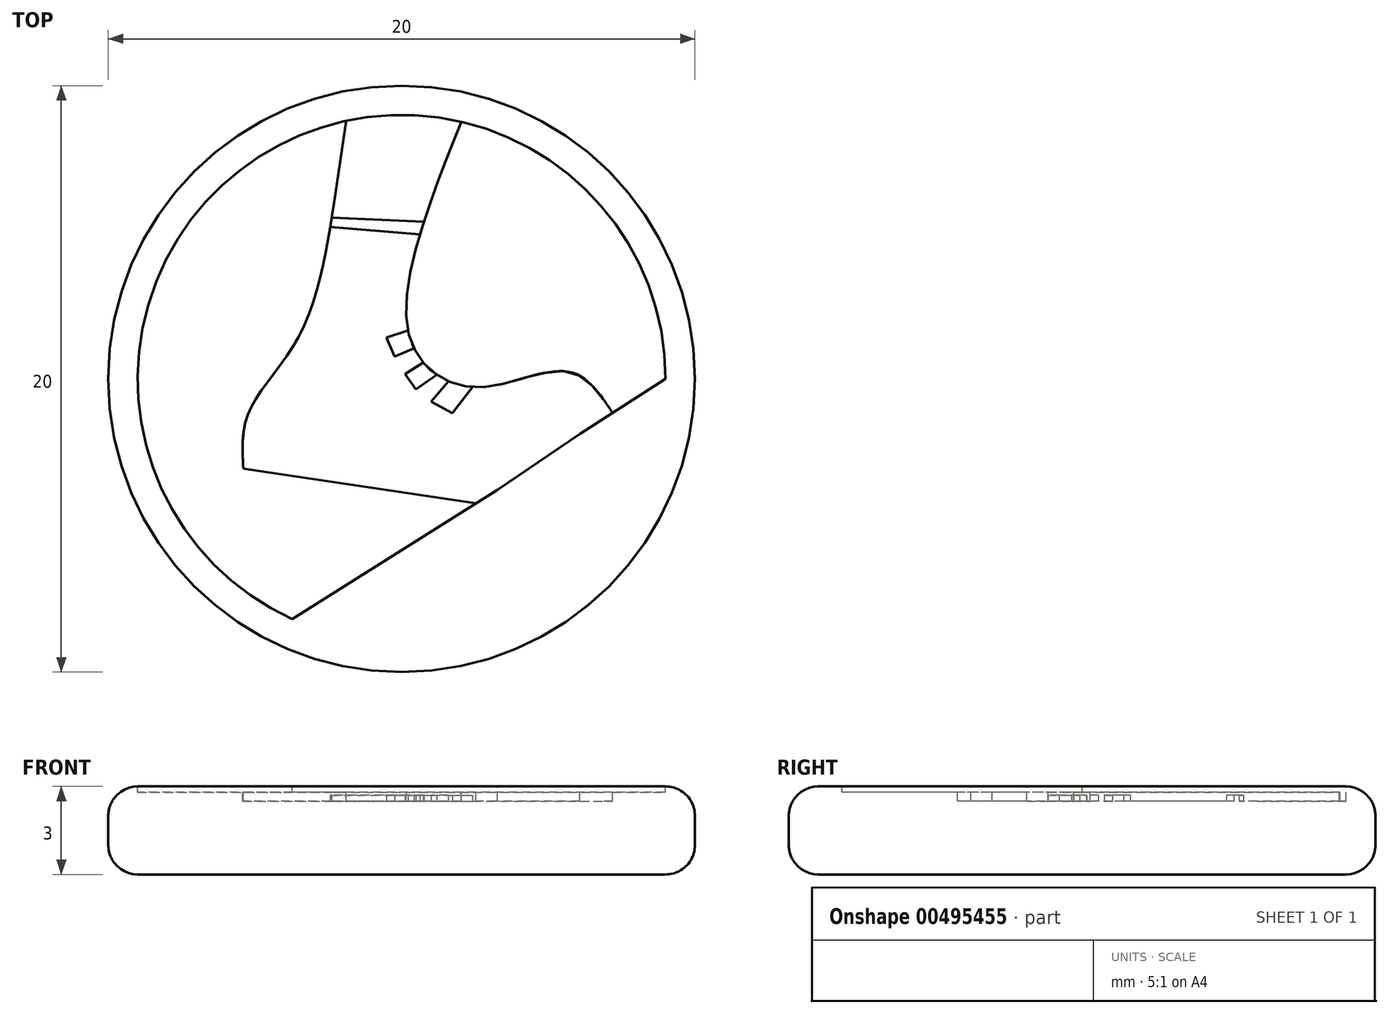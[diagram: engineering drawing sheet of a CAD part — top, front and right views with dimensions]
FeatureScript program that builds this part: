
annotation { "Feature Type Name" : "Feature", "Feature Type Description" : "" }
export const myFeature = defineFeature(function(context is Context, id is Id, definition is map)
    precondition{}
    {
        {
            var Q0;
            Q0=qCreatedBy(makeId("Top.planeOp"),FACE);
            var sketch = newSketch(context, id + "F0", { "sketchPlane" : qUnion([Q0])});
            skCircle(sketch, "E0", {"center": v(0, 0) * mm, "radius": 10 * mm});
            skSolve(sketch);
        }
        {
            var Q0;
            Q0=makeQuery(id+"F0.imprint","IMPRINT",FACE,{"disambiguationData":[TD([[makeQuery(id+"F0.imprint","IMPRINT",EDGE,{"derivedFrom":sQuery(id+"F0.wireOp",EDGE,"E0")}),1.0]])]});
            extrude(context, id + "F1", {"entities" : qUnion([Q0]), "depth" : 3 * mm});
        }
        {
            var Q0;
            Q0=makeQuery(id+"F1.opExtrude","CAP_EDGE",EDGE,{"disambiguationData":[OSD([sQuery(id+"F0.wireOp",EDGE,"E0")])],"isStart":false});
            var Q1;
            Q1=makeQuery(id+"F1.opExtrude","CAP_EDGE",EDGE,{"disambiguationData":[OSD([sQuery(id+"F0.wireOp",EDGE,"E0")])],"isStart":true});
            fillet(context, id + "F2", {"entities" : qUnion([Q0, Q1]), "radius" : 1 * mm, "tangentPropagation" : true, "allowEdgeOverflow" : false});
        }
        {
            var Q0;
            Q0=makeQuery(id+"F1.opExtrude","CAP_FACE",FACE,{"disambiguationData":[OSD([sQuery(id+"F0.wireOp",EDGE,"E0")])],"isStart":false});
            var sketch = newSketch(context, id + "F3", { "sketchPlane" : qUnion([Q0])});
            skLineSegment(sketch, "E1", {"start": v(6.08, -1.89) * mm, "end": v(3.26, -3.79) * mm});
            skLineSegment(sketch, "E2", {"start": v(3.26, -3.79) * mm, "end": v(-3.73, -8.2) * mm});
            skLineSegment(sketch, "E3", {"start": v(6.08, -1.89) * mm, "end": v(9, 0) * mm});
            skLineSegment(sketch, "E4", {"start": v(-2.31, 5.96) * mm, "end": v(-1.89, 8.8) * mm});
            skFitSpline(sketch, "E5", {"points": [v(2.04, 8.77) * mm, v(0.84, 5.6) * mm, v(0.17, 1.94) * mm, v(1.06, 0.24) * mm, v(2.92, -0.27) * mm, v(5.7, 0.24) * mm, v(7.2, -1.17) * mm], "startDerivative": vector(-6.42, -15.8) * mm, "endDerivative": vector(8.46, -12.94) * mm});
            skFitSpline(sketch, "E6", {"points": [v(-1.89, 8.8) * mm, v(-2.31, 5.96) * mm, v(-3.45, 1.55) * mm, v(-5.2, -1.13) * mm, v(-5.4, -3.06) * mm], "startDerivative": vector(-1.62, -10.82) * mm, "endDerivative": vector(0.58, -9.81) * mm});
            skLineSegment(sketch, "E7", {"start": v(-5.4, -3.06) * mm, "end": v(2.53, -4.25) * mm});
            skLineSegment(sketch, "E8", {"start": v(-5.41, -2.04) * mm, "end": v(2.62, -3.38) * mm});
            skLineSegment(sketch, "E9", {"start": v(2.62, -3.38) * mm, "end": v(6.88, -0.7) * mm});
            skSolve(sketch);
        }
        {
            var Q0;
            {var subQ0=sQuery(id+"F3.wireOp",EDGE,"E8");Q0=makeQuery(id+"F3.imprint","IMPRINT",FACE,{"disambiguationData":[TD([[makeQuery(id+"F3.imprint","IMPRINT",EDGE,{"derivedFrom":subQ0}),1.0]])]});}
            extrude(context, id + "F4", {"entities" : qUnion([Q0]), "operationType" : NewBodyOperationType.REMOVE, "oppositeDirection" : true, "depth" : 0.5 * mm});
        }
        {
            var Q0;
            {var subQ1=sQuery(id+"F3.wireOp",EDGE,"E1");Q0=makeQuery(id+"F3.imprint","IMPRINT",FACE,{"disambiguationData":[TD([[makeQuery(id+"F3.imprint","IMPRINT",EDGE,{"derivedFrom":subQ1}),-1.0]])]});}
            extrude(context, id + "F5", {"entities" : qUnion([Q0]), "operationType" : NewBodyOperationType.REMOVE, "oppositeDirection" : true, "depth" : 0.5 * mm, "offsetDistance" : 25 * mm});
        }
        {
            var Q0;
            Q0=makeQuery(id+"F4.boolean.opBoolean","COPY",FACE,{"derivedFrom":makeQuery(id+"F4.opExtrude","CAP_FACE",FACE,{"disambiguationData":[OSD([sQuery(id+"F0.wireOp",EDGE,"E0"),sQuery(id+"F3.wireOp",EDGE,"E5"),sQuery(id+"F3.wireOp",EDGE,"E6"),sQuery(id+"F3.wireOp",EDGE,"E8"),sQuery(id+"F3.wireOp",EDGE,"E9")])],"isStart":false})});
            var sketch = newSketch(context, id + "F6", { "sketchPlane" : qUnion([Q0])});
            skLineSegment(sketch, "E10", {"start": v(-3.1, 5.23) * mm, "end": v(1.62, 4.84) * mm});
            skLineSegment(sketch, "E11", {"start": v(1.62, 4.84) * mm, "end": v(1.66, 5.32) * mm});
            skLineSegment(sketch, "E12", {"start": v(1.66, 5.32) * mm, "end": v(-3.06, 5.53) * mm});
            skLineSegment(sketch, "E13", {"start": v(-3.06, 5.53) * mm, "end": v(-3.1, 5.23) * mm});
            skSolve(sketch);
        }
        {
            var Q0;
            {var subQ0=sQuery(id+"F6.wireOp",EDGE,"E10");var subQ1=makeQuery(id+"F4.boolean.opBoolean","COPY",EDGE,{"derivedFrom":makeQuery(id+"F4.opExtrude","CAP_EDGE",EDGE,{"disambiguationData":[OSD([sQuery(id+"F3.wireOp",EDGE,"E6")])],"isStart":false})});var subQ2=makeQuery(id+"F6.imprint","INTERSECT",VERTEX,{"derivedFrom":[subQ1,subQ0]});Q0=makeQuery(id+"F6.imprint","IMPRINT",FACE,{"disambiguationData":[TD([[makeQuery(id+"F6.imprint","IMPRINT",EDGE,{"disambiguationData":[TD([[subQ2,-1.0]])],"derivedFrom":subQ0}),1.0]])]});}
            extrude(context, id + "F7", {"entities" : qUnion([Q0]), "operationType" : NewBodyOperationType.ADD, "depth" : 0.2 * mm});
        }
        {
            var Q0;
            {var subQ0=sQuery(id+"F3.wireOp",EDGE,"E7");Q0=makeQuery(id+"F3.imprint","IMPRINT",FACE,{"disambiguationData":[TD([[makeQuery(id+"F3.imprint","IMPRINT",EDGE,{"derivedFrom":subQ0}),-1.0]])]});}
            var Q1;
            {var subQ0=sQuery(id+"F3.wireOp",EDGE,"E3");var subQ4=sQuery(id+"F3.wireOp",EDGE,"E5");var subQ5=makeQuery(id+"F3.imprint","INTERSECT",VERTEX,{"derivedFrom":[subQ0,subQ4]});Q1=makeQuery(id+"F3.imprint","IMPRINT",FACE,{"disambiguationData":[TD([[makeQuery(id+"F3.imprint","IMPRINT",EDGE,{"disambiguationData":[TD([[subQ5,1.0]])],"derivedFrom":subQ4}),1.0]])]});}
            extrude(context, id + "F8", {"entities" : qUnion([Q0, Q1]), "operationType" : NewBodyOperationType.REMOVE, "oppositeDirection" : true, "depth" : 0.2 * mm});
        }
        {
            var Q0;
            {var subQ0=sQuery(id+"F3.wireOp",EDGE,"E5");var subQ1=sQuery(id+"F3.wireOp",EDGE,"E6");var subQ2=sQuery(id+"F3.wireOp",EDGE,"E3");var subQ3=sQuery(id+"F3.wireOp",EDGE,"E1");var subQ4=sQuery(id+"F3.wireOp",EDGE,"E2");var subQ5=sQuery(id+"F3.wireOp",EDGE,"E7");var subQ6=sQuery(id+"F3.wireOp",EDGE,"E9");var subQ7=sQuery(id+"F3.wireOp",EDGE,"E8");Q0=makeQuery(id+"F7.boolean.opBoolean","SPLIT",FACE,{"disambiguationData":[TD([makeQuery(id+"F5.boolean.opBoolean","COPY",FACE,{"derivedFrom":makeQuery(id+"F5.opExtrude","SWEPT_FACE",FACE,{"disambiguationData":[OSD([subQ3])]})})])],"derivedFrom":makeQuery(id+"F5.boolean.opBoolean","MERGE",FACE,{"derivedFrom":[makeQuery(id+"F4.boolean.opBoolean","COPY",FACE,{"derivedFrom":makeQuery(id+"F4.opExtrude","CAP_FACE",FACE,{"disambiguationData":[OSD([sQuery(id+"F0.wireOp",EDGE,"E0"),subQ0,subQ1,subQ7,subQ6])],"isStart":false})}),makeQuery(id+"F5.opExtrude","CAP_FACE",FACE,{"disambiguationData":[OSD([subQ3,subQ4,subQ2,subQ0,subQ1,subQ5,subQ7,subQ6])],"isStart":false})]})});}
            var sketch = newSketch(context, id + "F9", { "sketchPlane" : qUnion([Q0])});
            skLineSegment(sketch, "E14", {"start": v(0.21, 1.65) * mm, "end": v(-0.51, 1.41) * mm});
            skLineSegment(sketch, "E15", {"start": v(-0.51, 1.41) * mm, "end": v(-0.24, 0.76) * mm});
            skLineSegment(sketch, "E16", {"start": v(-0.24, 0.76) * mm, "end": v(0.42, 1.04) * mm});
            skLineSegment(sketch, "E17", {"start": v(0.74, 0.56) * mm, "end": v(0.12, 0.16) * mm});
            skLineSegment(sketch, "E18", {"start": v(0.12, 0.16) * mm, "end": v(0.49, -0.36) * mm});
            skLineSegment(sketch, "E19", {"start": v(0.49, -0.36) * mm, "end": v(1.2, 0.14) * mm});
            skLineSegment(sketch, "E20", {"start": v(1.6, -0.09) * mm, "end": v(1, -0.78) * mm});
            skLineSegment(sketch, "E21", {"start": v(1, -0.78) * mm, "end": v(1.73, -1.17) * mm});
            skLineSegment(sketch, "E22", {"start": v(1.73, -1.17) * mm, "end": v(2.42, -0.29) * mm});
            skLineSegment(sketch, "E23", {"start": v(0.21, 1.65) * mm, "end": v(0.42, 1.04) * mm});
            skLineSegment(sketch, "E24", {"start": v(0.74, 0.56) * mm, "end": v(1.2, 0.14) * mm});
            skLineSegment(sketch, "E25", {"start": v(1.6, -0.09) * mm, "end": v(2.42, -0.29) * mm});
            skSolve(sketch);
        }
        {
            var Q0;
            Q0 = qSketchRegion(id + "F9", true);
            extrude(context, id + "F10", {"entities" : qUnion([Q0]), "operationType" : NewBodyOperationType.ADD, "depth" : 0.2 * mm, "offsetDistance" : 25 * mm});
        }
    });
